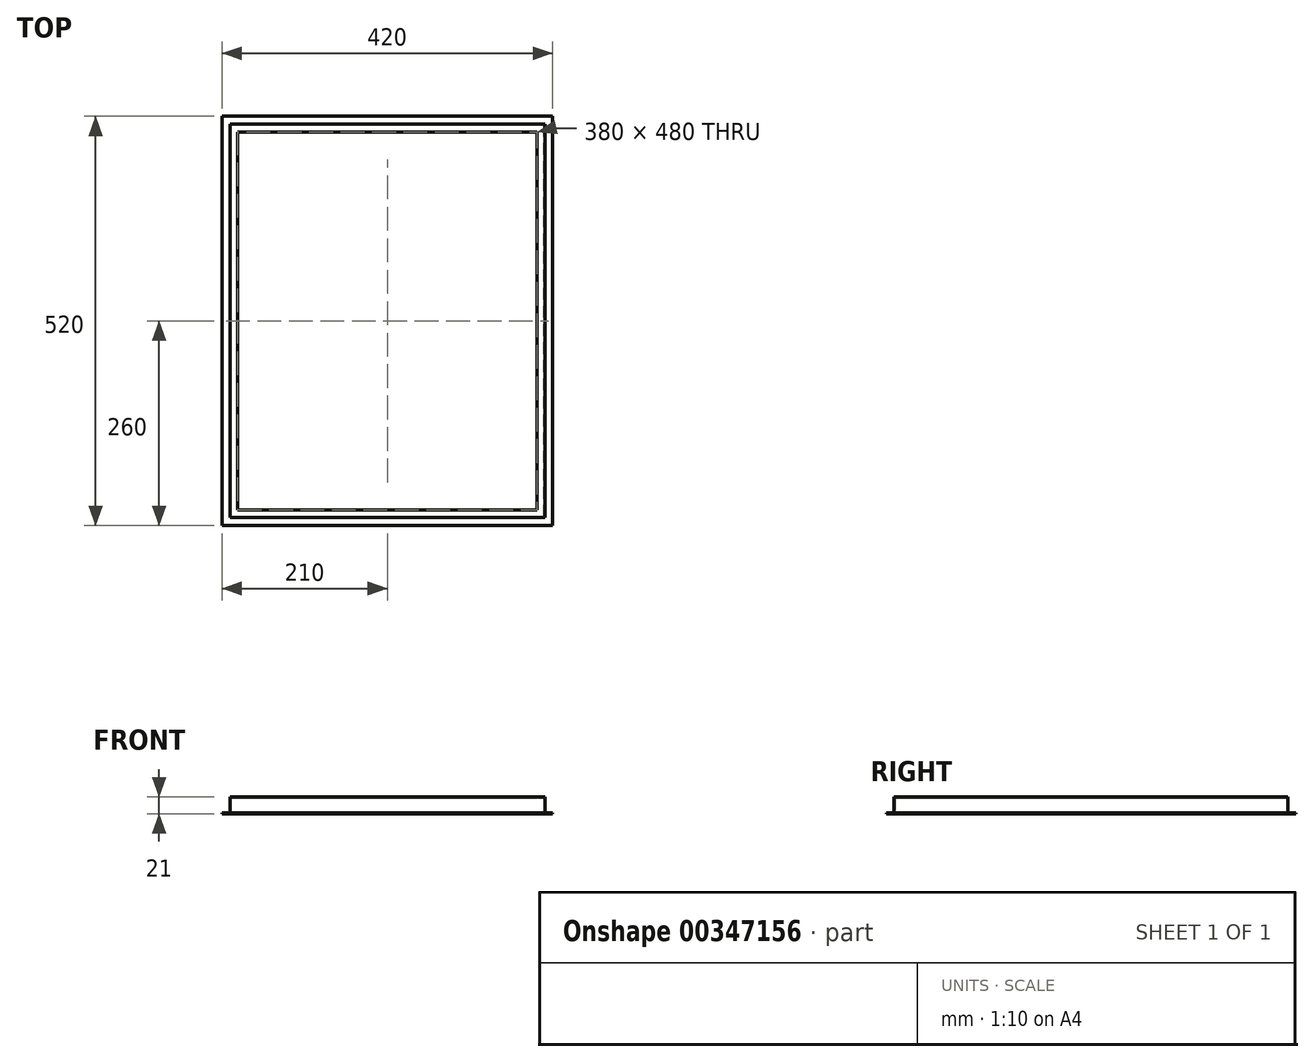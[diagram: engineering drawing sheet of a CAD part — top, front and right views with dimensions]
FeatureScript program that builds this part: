
annotation { "Feature Type Name" : "Feature", "Feature Type Description" : "" }
export const myFeature = defineFeature(function(context is Context, id is Id, definition is map)
    precondition{}
    {
        {
            var Q0;
            Q0=qCreatedBy(makeId("Right.planeOp"),FACE);
            var sketch = newSketch(context, id + "F0", { "sketchPlane" : qUnion([Q0])});
            skLineSegment(sketch, "E0", {"start": v(0, 0) * mm, "end": v(-10, 0) * mm});
            skLineSegment(sketch, "E1", {"start": v(-10, 0) * mm, "end": v(-10, -20) * mm});
            skLineSegment(sketch, "E2", {"start": v(-10, -20) * mm, "end": v(-20, -20) * mm});
            skLineSegment(sketch, "E3.0", {"start": v(0, -1) * mm, "end": v(-9, -1) * mm});
            skLineSegment(sketch, "E4.0", {"start": v(-9, -1) * mm, "end": v(-9, -21) * mm});
            skLineSegment(sketch, "E5.0", {"start": v(-9, -21) * mm, "end": v(-20, -21) * mm});
            skLineSegment(sketch, "E6", {"start": v(0, 0) * mm, "end": v(0, -1) * mm});
            skLineSegment(sketch, "E7", {"start": v(-20, -20) * mm, "end": v(-20, -21) * mm});
            skSolve(sketch);
        }
        {
            var Q0;
            Q0=qCreatedBy(makeId("Top.planeOp"),FACE);
            var sketch = newSketch(context, id + "F1", { "sketchPlane" : qUnion([Q0])});
            skLineSegment(sketch, "E8.0", {"start": v(0, 0) * mm, "end": v(0, -10) * mm, "construction": true});
            skLineSegment(sketch, "E9", {"start": v(0, -10) * mm, "end": v(200, -10) * mm});
            skLineSegment(sketch, "E10", {"start": v(200, -10) * mm, "end": v(200, 490) * mm});
            skLineSegment(sketch, "E11", {"start": v(200, 490) * mm, "end": v(-200, 490) * mm});
            skLineSegment(sketch, "E12", {"start": v(-200, 490) * mm, "end": v(-200, -10) * mm});
            skLineSegment(sketch, "E13", {"start": v(-200, -10) * mm, "end": v(0, -10) * mm});
            skSolve(sketch);
        }
        {
            var Q0;
            Q0 = qSketchRegion(id + "F0", true);
            var Q1;
            Q1 = qConstructionFilter(qBodyType(qCreatedBy(id + "F1" ,EDGE), BodyType.WIRE), ConstructionObject.NO);
            sweep(context, id + "F2", {"profiles" : qUnion([Q0]), "path" : qUnion([Q1])});
        }
    });
